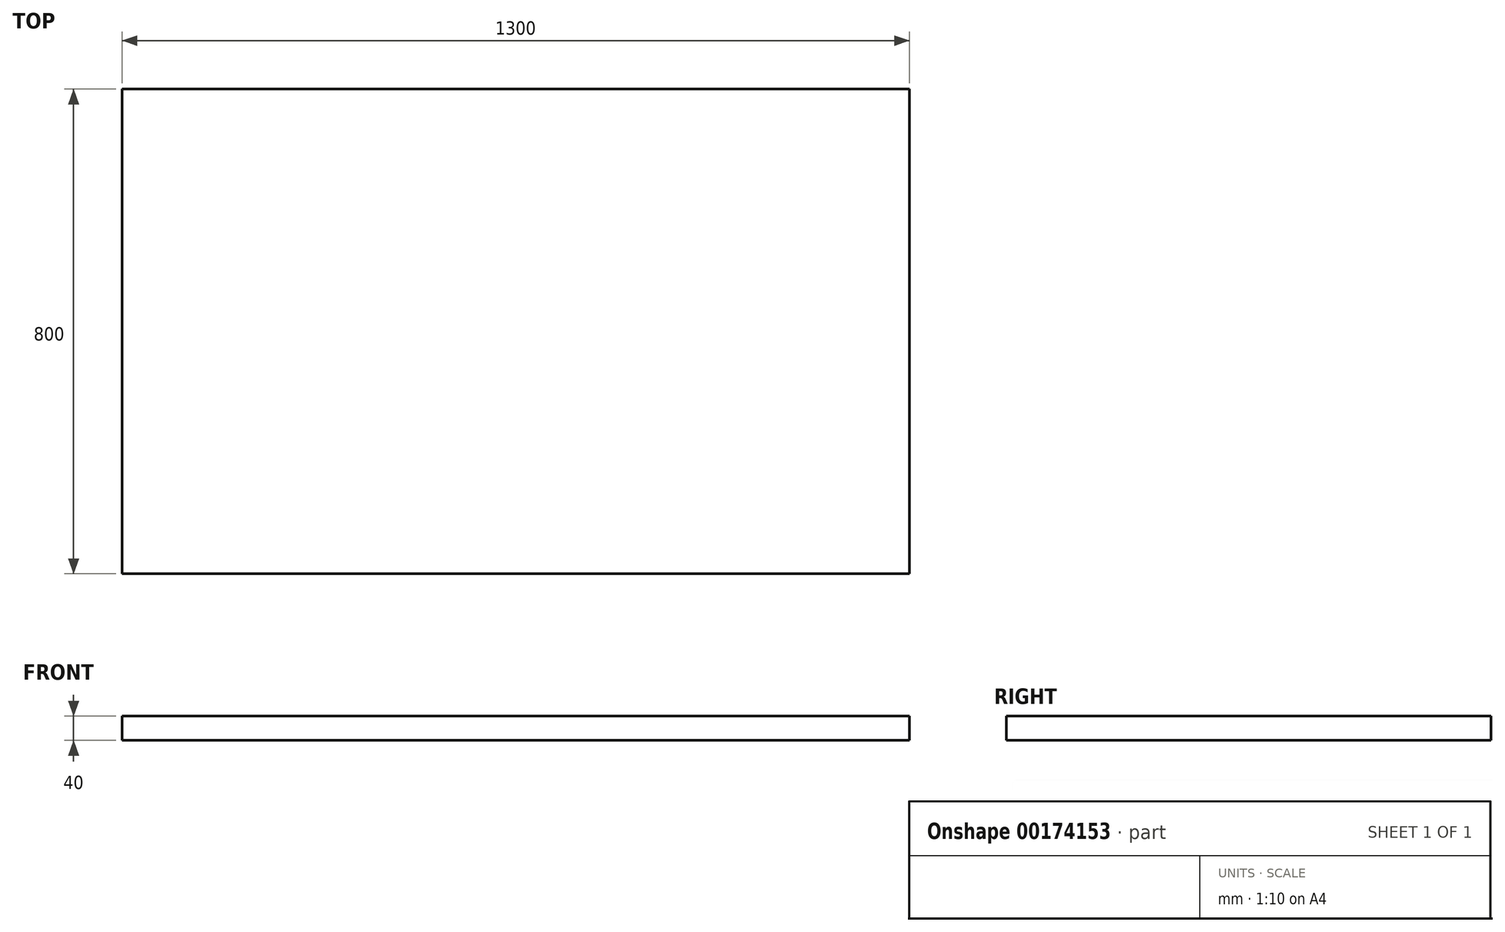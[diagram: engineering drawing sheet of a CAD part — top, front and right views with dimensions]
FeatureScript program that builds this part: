
annotation { "Feature Type Name" : "Feature", "Feature Type Description" : "" }
export const myFeature = defineFeature(function(context is Context, id is Id, definition is map)
    precondition{}
    {
        {
            var Q0;
            Q0=qCreatedBy(makeId("Top.planeOp"),FACE);
            var sketch = newSketch(context, id + "F0", { "sketchPlane" : qUnion([Q0])});
            skLineSegment(sketch, "E0.bottom", {"start": v(0, 0) * mm, "end": v(1300, 0) * mm});
            skLineSegment(sketch, "E0.top", {"start": v(0, 800) * mm, "end": v(1300, 800) * mm});
            skLineSegment(sketch, "E0.left", {"start": v(0, 0) * mm, "end": v(0, 800) * mm});
            skLineSegment(sketch, "E0.right", {"start": v(1300, 0) * mm, "end": v(1300, 800) * mm});
            skSolve(sketch);
        }
        {
            var Q0;
            Q0=makeQuery(id+"F0.imprint","IMPRINT",FACE,{"disambiguationData":[TD([[makeQuery(id+"F0.imprint","IMPRINT",EDGE,{"derivedFrom":sQuery(id+"F0.wireOp",EDGE,"E0.bottom")}),1.0]])]});
            extrude(context, id + "F1", {"entities" : qUnion([Q0]), "oppositeDirection" : true, "depth" : 40 * mm});
        }
    });
